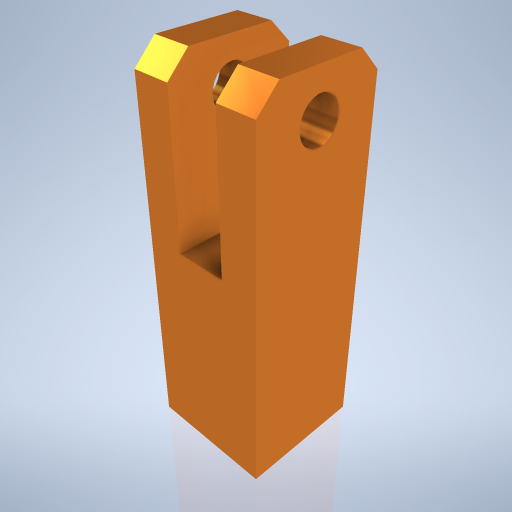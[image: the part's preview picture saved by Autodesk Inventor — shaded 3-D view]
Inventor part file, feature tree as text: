
AUTODESK INVENTOR PART (.ipt)
format: ipt  version: 2024.2 (Build 282272000, 272)  size: 259,584 bytes
history: native  units: mm
features: sketch x4, extrude x2, hole x2, mirror x1, chamfer x1
ambient origin geometry x8: Origin, YZ Plane, XZ Plane, XY Plane, X Axis, Y Axis, Z Axis, Center Point
bodies: Volumenkörper1 (feature_tree)
feature tree (10):
  extrude  "Extrusion1"  Depth=3.0mm
  extrude  "Extrusion2"  Depth=1.2mm
  hole  "Bohrung1"  [1 undecoded]
  mirror  "Spiegeln1"
  hole  "Bohrung2"  [1 undecoded]
  chamfer  "Fasen1"  [1 undecoded]
  sketch  "Skizze1"  dims[d0=3.0mm d1=3.0mm]
  sketch  "Skizze2"  dims[d2=9.0mm d3=0.0mm d4=1.2mm]
  sketch  "Skizze3"  dims[d5=4.0mm d6=0.0mm]
  sketch  "Skizze4"  dims[d7=1.0mm d8=6.0mm d9=4.0mm d10=2.0mm d11=90.0deg d12=8.0mm d13=0.0mm d14=8.0mm d15=1.5mm d16=6.0mm d17=4.0mm d18=2.0mm d19=90.0deg d20=2.5mm d21=20.594885mm d22=0.5mm d23=2.0mm d24=45.0deg]
note: 3 required parameter values undecoded (feature->parameter linkage not recoverable at this tier; creation-order binding heuristic only, values carry confidence <= 0.55)
